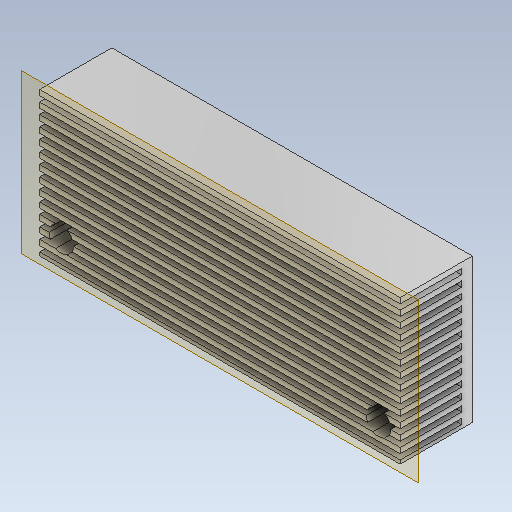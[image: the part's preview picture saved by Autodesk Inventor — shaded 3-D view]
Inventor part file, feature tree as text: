
AUTODESK INVENTOR PART (.ipt)
format: ipt  version: 2021 (Build 250183000, 183)  size: 268,800 bytes
history: native  units: in
note: dims shown in document units (in); Inventor stores cm internally (conversion verified against a paired STEP export)
features: sketch x3, extrude x2, pattern_linear x1, plane x1, hole x1, projected_geometry x1
ambient origin geometry x8: Origin, YZ Plane, XZ Plane, XY Plane, X Axis, Y Axis, Z Axis, Center Point
bodies: Solid1 (feature_tree)
feature tree (9):
  extrude  "Extrusion1"  Depth=1.5748in
  extrude  "Extrusion2"  Depth=0.0591in
  pattern_linear  "Rectangular Pattern1"  Spacing1=0.6693in  [1 undecoded]
  plane  "Work Plane1"
  hole  "Hole2"  [1 undecoded]
  sketch  "Sketch1"  dims[d0=3.937in d1=1.5748in]
  sketch  "Sketch2"  dims[d2=0.7874in d3=0.0in d4=0.0591in]
  projected_geometry  "Projected Loop1"
  sketch  "Sketch4"  dims[d6=0.0591in d7=0.6693in d8=0.0in d9=5.1181in d11=0.1181in d21=0.7874in d22=0.2362in d23=0.266in d24=0.2362in d25=0.4375in d26=0.6693in d27=0.5635in d28=0.12in d29=0.0in d30=0.2756in d31=0.2756in d32=0.2362in]
note: 2 required parameter values undecoded (feature->parameter linkage not recoverable at this tier; creation-order binding heuristic only, values carry confidence <= 0.55)
